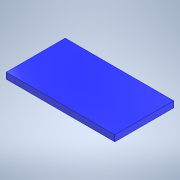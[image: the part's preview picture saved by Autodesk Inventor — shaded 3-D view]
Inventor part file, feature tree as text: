
AUTODESK INVENTOR PART (.ipt)
format: ipt  version: 2020 (Build 240168000, 168)  size: 93,184 bytes
history: native  units: in
note: dims shown in document units (in); Inventor stores cm internally (conversion verified against a paired STEP export)
features: extrude x1, sketch x1
ambient origin geometry x8: Origin, YZ Plane, XZ Plane, XY Plane, X Axis, Y Axis, Z Axis, Center Point
bodies: Solid1 (feature_tree)
feature tree (2):
  extrude  "Extrusion1"  Depth=1.45in
  sketch  "Sketch1"  dims[d0=2.67in d1=1.45in d2=0.15in d3=0.0in]
